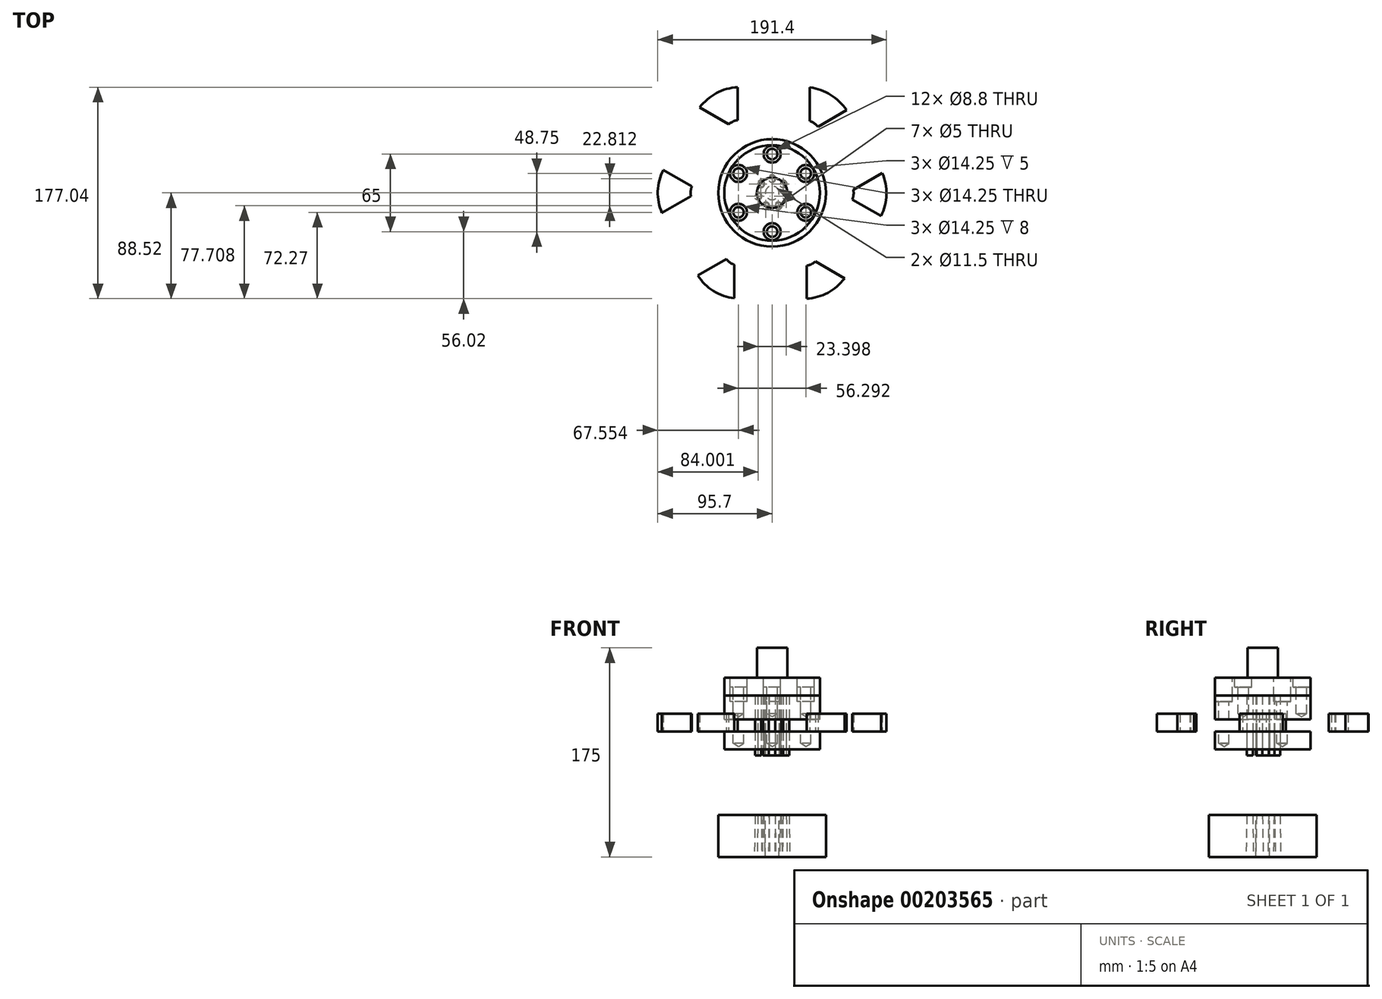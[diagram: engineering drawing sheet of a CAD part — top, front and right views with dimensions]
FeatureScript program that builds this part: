
annotation { "Feature Type Name" : "Feature", "Feature Type Description" : "" }
export const myFeature = defineFeature(function(context is Context, id is Id, definition is map)
    precondition{}
    {
        {
            var Q0;
            Q0=qCreatedBy(makeId("Top.planeOp"),FACE);
            var sketch = newSketch(context, id + "F0", { "sketchPlane" : qUnion([Q0])});
            skCircle(sketch, "E0", {"center": v(0, 0) * mm, "radius": 45 * mm});
            skCircle(sketch, "E1", {"center": v(0, 0) * mm, "radius": 12 * mm, "construction": true});
            skCircle(sketch, "E2", {"center": v(0, 0) * mm, "radius": 5.75 * mm});
            skSolve(sketch);
        }
        {
            var Q0;
            Q0 = qSketchRegion(id + "F0", true);
            extrude(context, id + "F1", {"entities" : qUnion([Q0]), "oppositeDirection" : true, "depth" : 35 * mm});
        }
        {
            var Q0;
            Q0=qCreatedBy(makeId("Top.planeOp"),FACE);
            var sketch = newSketch(context, id + "F2", { "sketchPlane" : qUnion([Q0])});
            skCircle(sketch, "E3.0", {"center": v(0, 0) * mm, "radius": 12 * mm, "construction": true});
            skCircle(sketch, "E4", {"center": v(0, 12) * mm, "radius": 2.5 * mm});
            skCircle(sketch, "E5.1.0", {"center": v(-9.38, 7.48) * mm, "radius": 2.5 * mm});
            skCircle(sketch, "E5.2.0", {"center": v(-11.7, -2.67) * mm, "radius": 2.5 * mm});
            skCircle(sketch, "E6.1.3.0", {"center": v(-5.2, -10.81) * mm, "radius": 2.5 * mm});
            skCircle(sketch, "E6.1.4.0", {"center": v(5.2, -10.81) * mm, "radius": 2.5 * mm});
            skCircle(sketch, "E6.1.5.0", {"center": v(11.7, -2.67) * mm, "radius": 2.5 * mm});
            skCircle(sketch, "E6.1.6.0", {"center": v(9.38, 7.48) * mm, "radius": 2.5 * mm});
            skSolve(sketch);
        }
        {
            var Q0;
            Q0 = qSketchRegion(id + "F2", true);
            extrude(context, id + "F3", {"entities" : qUnion([Q0]), "operationType" : NewBodyOperationType.REMOVE, "endBound" : BoundingType.UP_TO_NEXT, "oppositeDirection" : true, "depth" : 25 * mm, "hasDraft" : true, "draftAngle" : 1 * degree});
        }
        {
            var Q0;
            Q0=qCreatedBy(makeId("Top.planeOp"),FACE);
            cPlane(context, id + "F4", {"entities" : qUnion([Q0]), "cplaneType" : CPlaneType.OFFSET, "offset" : 50 * mm, "width" : 150 * mm, "height" : 150 * mm});
        }
        {
            var Q0;
            Q0=qCreatedBy(id+"F4.planeOp",FACE);
            var sketch = newSketch(context, id + "F5", { "sketchPlane" : qUnion([Q0])});
            skCircle(sketch, "E7.0", {"center": v(0, 0) * mm, "radius": 5.75 * mm});
            skCircle(sketch, "E8.0", {"center": v(0, 12) * mm, "radius": 2.5 * mm});
            skCircle(sketch, "E9.0", {"center": v(-9.38, 7.48) * mm, "radius": 2.5 * mm});
            skCircle(sketch, "E10.0", {"center": v(-11.7, -2.67) * mm, "radius": 2.5 * mm});
            skCircle(sketch, "E11.0", {"center": v(-5.2, -10.81) * mm, "radius": 2.5 * mm});
            skCircle(sketch, "E12.0", {"center": v(5.2, -10.81) * mm, "radius": 2.5 * mm});
            skCircle(sketch, "E13.0", {"center": v(11.7, -2.67) * mm, "radius": 2.5 * mm});
            skCircle(sketch, "E14.0", {"center": v(9.38, 7.48) * mm, "radius": 2.5 * mm});
            skSolve(sketch);
        }
        {
            var Q0;
            Q0 = qSketchRegion(id + "F5", true);
            extrude(context, id + "F6", {"entities" : qUnion([Q0]), "depth" : 50 * mm});
        }
        {
            var Q0;
            Q0=makeQuery(id+"F6.opExtrude","CAP_FACE",FACE,{"disambiguationData":[OSD([sQuery(id+"F5.wireOp",EDGE,"E7.0")])],"isStart":false});
            var sketch = newSketch(context, id + "F7", { "sketchPlane" : qUnion([Q0])});
            skCircle(sketch, "E15", {"center": v(0, 0) * mm, "radius": 40 * mm});
            skSolve(sketch);
        }
        {
            var Q0;
            Q0 = qSketchRegion(id + "F7", true);
            extrude(context, id + "F8", {"entities" : qUnion([Q0]), "oppositeDirection" : true, "depth" : 20 * mm});
        }
        {
            var Q0;
            Q0=makeQuery(id+"F8.opExtrude","CAP_FACE",FACE,{"disambiguationData":[OSD([sQuery(id+"F7.wireOp",EDGE,"E15")])],"isStart":true});
            var sketch = newSketch(context, id + "F9", { "sketchPlane" : qUnion([Q0])});
            skCircle(sketch, "E16.0", {"center": v(0, 0) * mm, "radius": 40 * mm});
            skSolve(sketch);
        }
        {
            var Q0;
            Q0=makeQuery(id+"F9.imprint","IMPRINT",FACE,{"disambiguationData":[TD([[makeQuery(id+"F9.imprint","IMPRINT",EDGE,{"derivedFrom":sQuery(id+"F9.wireOp",EDGE,"E16.0")}),1.0]])]});
            extrude(context, id + "F10", {"entities" : qUnion([Q0]), "depth" : 15 * mm});
        }
        {
            var Q0;
            Q0=makeQuery(id+"F10.opExtrude","CAP_FACE",FACE,{"disambiguationData":[OSD([sQuery(id+"F9.wireOp",EDGE,"E16.0")])],"isStart":false});
            var sketch = newSketch(context, id + "F11", { "sketchPlane" : qUnion([Q0])});
            skCircle(sketch, "E17", {"center": v(0, 0) * mm, "radius": 12.65 * mm});
            skSolve(sketch);
        }
        {
            var Q0;
            Q0 = qSketchRegion(id + "F11", true);
            extrude(context, id + "F12", {"entities" : qUnion([Q0]), "operationType" : NewBodyOperationType.ADD, "depth" : 25 * mm});
        }
        {
            var Q0;
            Q0=qCreatedBy(id+"F4.planeOp",FACE);
            cPlane(context, id + "F13", {"entities" : qUnion([Q0]), "cplaneType" : CPlaneType.OFFSET, "offset" : 5 * mm, "width" : 150 * mm, "height" : 150 * mm});
        }
        {
            var Q0;
            Q0=qCreatedBy(id+"F13.planeOp",FACE);
            var sketch = newSketch(context, id + "F14", { "sketchPlane" : qUnion([Q0])});
            skCircle(sketch, "E18.0", {"center": v(0, 0) * mm, "radius": 5.75 * mm});
            skCircle(sketch, "E19.0", {"center": v(0, 12) * mm, "radius": 2.5 * mm});
            skCircle(sketch, "E20.0", {"center": v(-9.38, 7.48) * mm, "radius": 2.5 * mm});
            skCircle(sketch, "E21.0", {"center": v(-11.7, -2.67) * mm, "radius": 2.5 * mm});
            skCircle(sketch, "E22.0", {"center": v(-5.2, -10.81) * mm, "radius": 2.5 * mm});
            skCircle(sketch, "E23.0", {"center": v(5.2, -10.81) * mm, "radius": 2.5 * mm});
            skCircle(sketch, "E24.0", {"center": v(11.7, -2.67) * mm, "radius": 2.5 * mm});
            skCircle(sketch, "E25.0", {"center": v(9.38, 7.48) * mm, "radius": 2.5 * mm});
            skCircle(sketch, "E26", {"center": v(0, 0) * mm, "radius": 40 * mm});
            skSolve(sketch);
        }
        {
            var Q0;
            Q0 = qSketchRegion(id + "F14", true);
            extrude(context, id + "F15", {"entities" : qUnion([Q0]), "depth" : 15 * mm});
        }
        {
            var Q0;
            Q0=makeQuery(id+"F15.opExtrude","CAP_FACE",FACE,{"disambiguationData":[OSD([sQuery(id+"F14.wireOp",EDGE,"E18.0"),sQuery(id+"F14.wireOp",EDGE,"E19.0"),sQuery(id+"F14.wireOp",EDGE,"E20.0"),sQuery(id+"F14.wireOp",EDGE,"E21.0"),sQuery(id+"F14.wireOp",EDGE,"E22.0"),sQuery(id+"F14.wireOp",EDGE,"E23.0"),sQuery(id+"F14.wireOp",EDGE,"E24.0"),sQuery(id+"F14.wireOp",EDGE,"E25.0"),sQuery(id+"F14.wireOp",EDGE,"E26")])],"isStart":false});
            cPlane(context, id + "F16", {"entities" : qUnion([Q0]), "cplaneType" : CPlaneType.OFFSET, "offset" : 0 * mm, "width" : 150 * mm, "height" : 150 * mm});
        }
        {
            var Q0;
            Q0=qCreatedBy(id+"F16.planeOp",FACE);
            var sketch = newSketch(context, id + "F17", { "sketchPlane" : qUnion([Q0])});
            skArc(sketch, "E27", {"start": v(11.74, 9.34) * mm, "mid": v(8.7, 12.22) * mm, "end": v(5, 14.14) * mm});
            skArc(sketch, "E28", {"start": v(35.64, 23.15) * mm, "mid": v(22.45, 36.09) * mm, "end": v(5, 42.2) * mm});
            skLineSegment(sketch, "E29.0", {"start": v(5, 14.14) * mm, "end": v(5, 42.2) * mm});
            skPoint(sketch, "E30.orphan", {"position": v(0, 15) * mm});
            skLineSegment(sketch, "E31.0", {"start": v(11.74, 9.34) * mm, "end": v(35.64, 23.15) * mm});
            skLineSegment(sketch, "E32", {"start": v(0, 0) * mm, "end": v(26.6, 46.07) * mm, "construction": true});
            skSolve(sketch);
        }
        {
            var Q0;
            Q0 = qSketchRegion(id + "F17", true);
            extrude(context, id + "F18", {"entities" : qUnion([Q0]), "depth" : 15 * mm});
        }
        {
            var Q0;
            Q0=makeQuery(id+"F18.opExtrude","SWEPT_BODY",BODY,{"disambiguationData":[OSD([sQuery(id+"F17.wireOp",EDGE,"E27"),sQuery(id+"F17.wireOp",EDGE,"E28"),sQuery(id+"F17.wireOp",EDGE,"E29.0"),sQuery(id+"F17.wireOp",EDGE,"E31.0")])]});
            var Q1;
            Q1=sQuery(id+"F17.wireOp",EDGE,"E32");
            transform(context, id + "F19", {"entities" : qUnion([Q0]), "transformType" : TransformType.TRANSLATION_ENTITY, "oppositeDirectionEntity" : false, "transformLine" : qUnion([Q1]), "makeCopy" : false});
        }
        {
            var Q0;
            Q0=makeQuery(id+"F18.opExtrude","SWEPT_BODY",BODY,{"disambiguationData":[OSD([sQuery(id+"F17.wireOp",EDGE,"E27"),sQuery(id+"F17.wireOp",EDGE,"E28"),sQuery(id+"F17.wireOp",EDGE,"E29.0"),sQuery(id+"F17.wireOp",EDGE,"E31.0")])]});
            var Q1;
            Q1=makeQuery(id+"F15.opExtrude","CAP_EDGE",EDGE,{"disambiguationData":[OSD([sQuery(id+"F14.wireOp",EDGE,"E26")])],"isStart":false});
            circularPattern(context, id + "F20", {"entities" : qUnion([Q0]), "axis" : qUnion([Q1]), "angle" : 360 * degree, "instanceCount" : 6, "equalSpace" : true});
        }
        {
            var Q0;
            Q0=makeQuery(id+"F10.opExtrude","CAP_FACE",FACE,{"disambiguationData":[OSD([sQuery(id+"F9.wireOp",EDGE,"E16.0")])],"isStart":false});
            var sketch = newSketch(context, id + "F21", { "sketchPlane" : qUnion([Q0])});
            skCircle(sketch, "E33", {"center": v(0, 0) * mm, "radius": 32.5 * mm, "construction": true});
            skLineSegment(sketch, "E34", {"start": v(0, 0) * mm, "end": v(0, -32.5) * mm, "construction": true});
            skLineSegment(sketch, "E35", {"start": v(0, 0) * mm, "end": v(28.15, 16.25) * mm, "construction": true});
            skLineSegment(sketch, "E36", {"start": v(0, 0) * mm, "end": v(-28.15, 16.25) * mm, "construction": true});
            skSolve(sketch);
        }
        {
            var Q0;
            Q0=sQuery(id+"F21.wireOp",VERTEX,"E34.end");
            var Q1;
            Q1=sQuery(id+"F21.wireOp",VERTEX,"E35.end");
            var Q2;
            Q2=sQuery(id+"F21.wireOp",VERTEX,"E36.end");
            var Q3;
            Q3=makeQuery(id+"F10.opExtrude","SWEPT_BODY",BODY,{"disambiguationData":[OSD([sQuery(id+"F9.wireOp",EDGE,"E16.0")])]});
            var Q4;
            Q4=makeQuery(id+"F8.opExtrude","SWEPT_BODY",BODY,{"disambiguationData":[OSD([sQuery(id+"F7.wireOp",EDGE,"E15")])]});
            var Q5;
            Q5=makeQuery(id+"F15.opExtrude","SWEPT_BODY",BODY,{"disambiguationData":[OSD([sQuery(id+"F14.wireOp",EDGE,"E18.0"),sQuery(id+"F14.wireOp",EDGE,"E19.0"),sQuery(id+"F14.wireOp",EDGE,"E20.0"),sQuery(id+"F14.wireOp",EDGE,"E21.0"),sQuery(id+"F14.wireOp",EDGE,"E22.0"),sQuery(id+"F14.wireOp",EDGE,"E23.0"),sQuery(id+"F14.wireOp",EDGE,"E24.0"),sQuery(id+"F14.wireOp",EDGE,"E25.0"),sQuery(id+"F14.wireOp",EDGE,"E26")])]});
            hole(context, id + "F22", {"style" : HoleStyle.C_BORE, "endStyle" : HoleEndStyle.BLIND, "holeDiameter" : 8.8 * mm, "cBoreDiameter" : 14.25 * mm, "cBoreDepth" : 20 * mm, "holeDepth" : 55 * mm, "tappedDepth" : 57 * mm, "tapClearance" : 3, "locations" : qUnion([Q0, Q1, Q2]), "scope" : qUnion([Q3, Q4, Q5])});
        }
        {
            var Q0;
            Q0=makeQuery(id+"F10.opExtrude","CAP_FACE",FACE,{"disambiguationData":[OSD([sQuery(id+"F9.wireOp",EDGE,"E16.0")])],"isStart":false});
            var sketch = newSketch(context, id + "F23", { "sketchPlane" : qUnion([Q0])});
            skCircle(sketch, "E37.0", {"center": v(0, 0) * mm, "radius": 32.5 * mm, "construction": true});
            skLineSegment(sketch, "E38", {"start": v(0, 0) * mm, "end": v(0, 32.5) * mm, "construction": true});
            skLineSegment(sketch, "E39", {"start": v(0, 0) * mm, "end": v(28.15, -16.25) * mm, "construction": true});
            skLineSegment(sketch, "E40", {"start": v(0, 0) * mm, "end": v(-28.15, -16.25) * mm, "construction": true});
            skSolve(sketch);
        }
        {
            var Q0;
            Q0=sQuery(id+"F23.wireOp",VERTEX,"E38.end");
            var Q1;
            Q1=sQuery(id+"F23.wireOp",VERTEX,"E40.end");
            var Q2;
            Q2=sQuery(id+"F23.wireOp",VERTEX,"E39.end");
            var Q3;
            Q3=makeQuery(id+"F10.opExtrude","SWEPT_BODY",BODY,{"disambiguationData":[OSD([sQuery(id+"F9.wireOp",EDGE,"E16.0")])]});
            var Q4;
            Q4=makeQuery(id+"F8.opExtrude","SWEPT_BODY",BODY,{"disambiguationData":[OSD([sQuery(id+"F7.wireOp",EDGE,"E15")])]});
            hole(context, id + "F24", {"style" : HoleStyle.C_BORE, "endStyle" : HoleEndStyle.BLIND, "standardTappedOrClearance" : lookupTablePath({ "standard" : "ISO", "fit" : "Normal", "size" : "M8", "type" : "Clearance" }), "standardBlindInLast" : lookupTablePath({ "fit" : "Standard", "standard" : "ISO", "size" : "M8", "type" : "Clearance" }), "holeDiameter" : 8.8 * mm, "cBoreDiameter" : 14.25 * mm, "cBoreDepth" : 8 * mm, "holeDepth" : 30 * mm, "tappedDepth" : 57 * mm, "tapClearance" : 3, "startFromSketch" : true, "locations" : qUnion([Q0, Q1, Q2]), "scope" : qUnion([Q3, Q4])});
        }
    });
